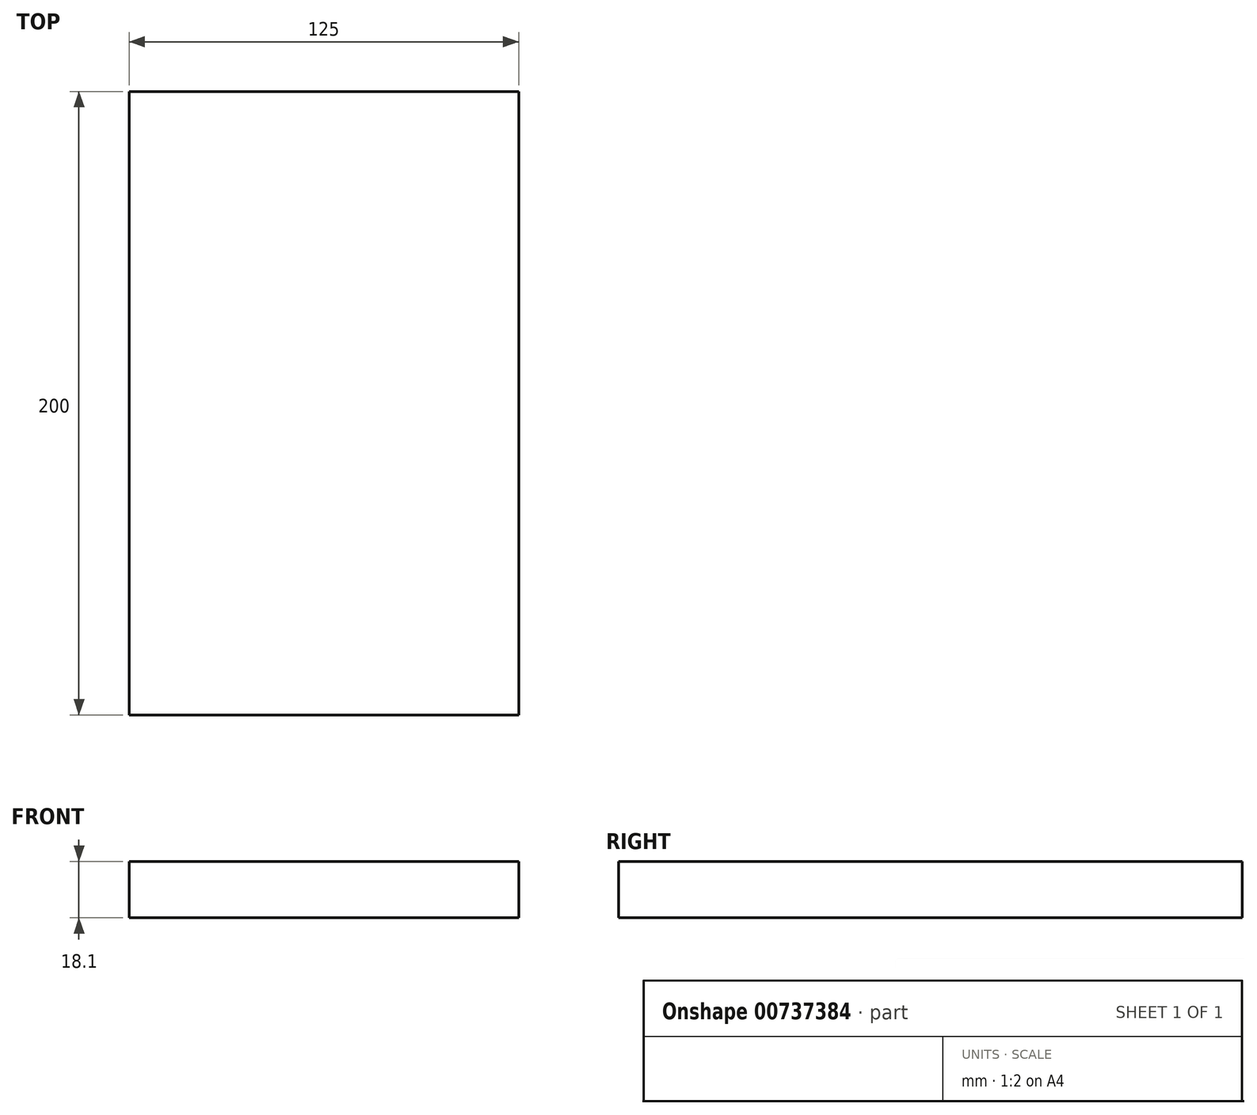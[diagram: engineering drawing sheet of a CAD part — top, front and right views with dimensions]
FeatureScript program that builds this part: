
annotation { "Feature Type Name" : "Feature", "Feature Type Description" : "" }
export const myFeature = defineFeature(function(context is Context, id is Id, definition is map)
    precondition{}
    {
        {
            var Q0;
            Q0=qCreatedBy(makeId("Top.planeOp"),FACE);
            var sketch = newSketch(context, id + "F0", { "sketchPlane" : qUnion([Q0])});
            skLineSegment(sketch, "E0.bottom", {"start": v(-62.5, 100) * mm, "end": v(62.5, 100) * mm});
            skLineSegment(sketch, "E0.top", {"start": v(-62.5, -100) * mm, "end": v(62.5, -100) * mm});
            skLineSegment(sketch, "E0.left", {"start": v(-62.5, 100) * mm, "end": v(-62.5, -100) * mm});
            skLineSegment(sketch, "E0.right", {"start": v(62.5, 100) * mm, "end": v(62.5, -100) * mm});
            skPoint(sketch, "E0.middle", {"position": v(0, 0) * mm});
            skSolve(sketch);
        }
        {
            var Q0;
            Q0=makeQuery(id+"F0.imprint","IMPRINT",FACE,{"disambiguationData":[TD([[makeQuery(id+"F0.imprint","IMPRINT",EDGE,{"derivedFrom":sQuery(id+"F0.wireOp",EDGE,"E0.bottom")}),-1.0]])]});
            extrude(context, id + "F1", {"entities" : qUnion([Q0]), "depth" : 18.1 * mm, "offsetDistance" : 25 * mm});
        }
    });
